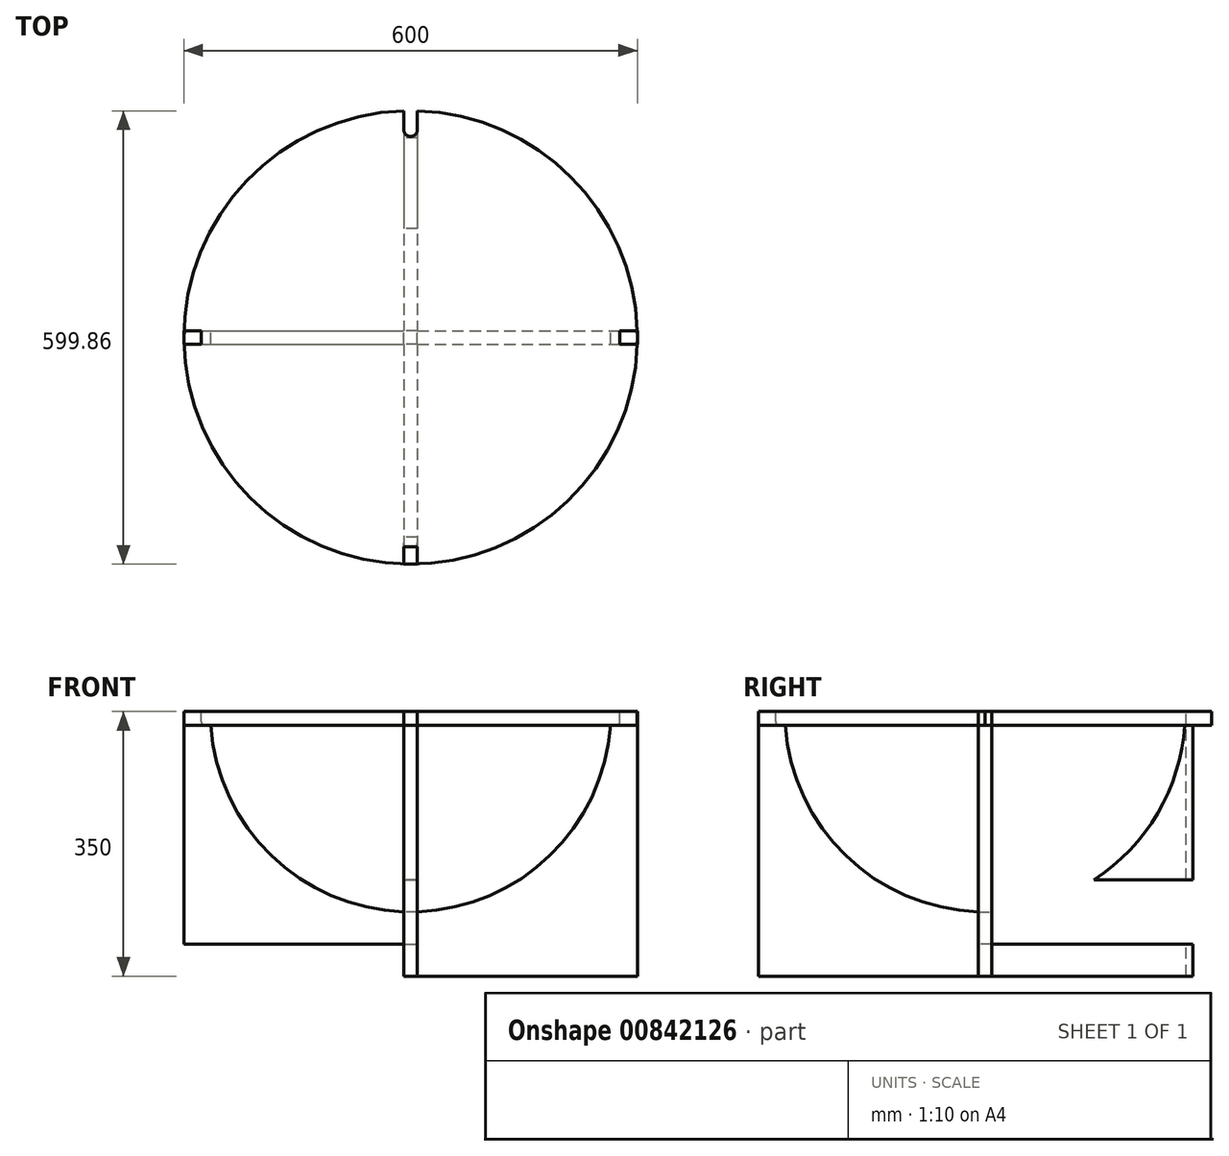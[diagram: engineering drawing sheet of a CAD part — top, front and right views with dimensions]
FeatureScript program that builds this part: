
annotation { "Feature Type Name" : "Feature", "Feature Type Description" : "" }
export const myFeature = defineFeature(function(context is Context, id is Id, definition is map)
    precondition{}
    {
        {
            var Q0;
            Q0=qCreatedBy(makeId("Front.planeOp"),FACE);
            var sketch = newSketch(context, id + "F0", { "sketchPlane" : qUnion([Q0])});
            skLineSegment(sketch, "E0.bottom", {"start": v(-300, -175) * mm, "end": v(140, -175) * mm});
            skLineSegment(sketch, "E0.top", {"start": v(-300, 175) * mm, "end": v(-277, 175) * mm});
            skLineSegment(sketch, "E0.left", {"start": v(-300, -175) * mm, "end": v(-300, 175) * mm});
            skLineSegment(sketch, "E0.right", {"start": v(300, -175) * mm, "end": v(300, 175) * mm});
            skPoint(sketch, "E0.middle", {"position": v(0, 0) * mm});
            skArc(sketch, "E1", {"start": v(-264.39, 157) * mm, "mid": v(0, -90) * mm, "end": v(264.39, 157) * mm});
            skLineSegment(sketch, "E2.trimOffspring", {"start": v(277, 175) * mm, "end": v(300, 175) * mm});
            skLineSegment(sketch, "E3.trimOffspring", {"start": v(140, -175) * mm, "end": v(300, -175) * mm});
            skLineSegment(sketch, "E4.bottom", {"start": v(-277, 157) * mm, "end": v(-264.39, 157) * mm});
            skLineSegment(sketch, "E4.left", {"start": v(-277, 157) * mm, "end": v(-277, 175) * mm});
            skLineSegment(sketch, "E4.right", {"start": v(277, 157) * mm, "end": v(277, 175) * mm});
            skPoint(sketch, "E5.orphan", {"position": v(-277, 193) * mm});
            skLineSegment(sketch, "E6.trimOffspring", {"start": v(264.39, 157) * mm, "end": v(277, 157) * mm});
            skPoint(sketch, "E7.orphan", {"position": v(277, 193) * mm});
            skSolve(sketch);
        }
        {
            var Q0;
            Q0=qSketchRegion(id+"F0",true);
            extrude(context, id + "F1", {"entities" : qUnion([Q0]), "depth" : 9 * mm, "offsetDistance" : 25 * mm, "hasSecondDirection" : true, "secondDirectionOppositeDirection" : true, "secondDirectionDepth" : 9 * mm});
        }
        {
            var Q0;
            Q0=qCreatedBy(makeId("Right.planeOp"),FACE);
            var Q1;
            Q1=qCreatedBy(makeId("Front.planeOp"),FACE);
            cPlane(context, id + "F2", {"entities" : qUnion([Q0, Q1]), "cplaneType" : CPlaneType.MID_PLANE, "offset" : 25 * mm, "width" : 150 * mm, "height" : 150 * mm});
        }
        {
            var Q0;
            Q0=makeQuery(id+"F1.opExtrude","SWEPT_BODY",BODY,{"disambiguationData":[OSD([sQuery(id+"F0.wireOp",EDGE,"E0.bottom"),sQuery(id+"F0.wireOp",EDGE,"E0.top"),sQuery(id+"F0.wireOp",EDGE,"E0.left"),sQuery(id+"F0.wireOp",EDGE,"E0.right"),sQuery(id+"F0.wireOp",EDGE,"E1"),sQuery(id+"F0.wireOp",EDGE,"EXiE6QKu-Vo7E-oY48-lKYo-ds7yFPW4EHc2"),sQuery(id+"F0.wireOp",EDGE,"E2.trimOffspring"),sQuery(id+"F0.wireOp",EDGE,"E3.trimOffspring")])]});
            var Q1;
            Q1=qCreatedBy(id+"F2.planeOp",FACE);
            mirror(context, id + "F3", {"entities" : qUnion([Q0]), "mirrorPlane" : qUnion([Q1])});
        }
        {
            var Q0;
            Q0=makeQuery(id+"F1.opExtrude","SWEPT_FACE",FACE,{"disambiguationData":[OSD([sQuery(id+"F0.wireOp",EDGE,"E2.trimOffspring")])]});
            var sketch = newSketch(context, id + "F4", { "sketchPlane" : qUnion([Q0])});
            skCircle(sketch, "E8", {"center": v(0, 0) * mm, "radius": 300 * mm});
            skSolve(sketch);
        }
        {
            var Q0;
            {var subQ1=sQuery(id+"F0.wireOp",EDGE,"E2.trimOffspring");var subQ6=makeQuery(id+"F1.opExtrude","SWEPT_EDGE",EDGE,{"disambiguationData":[OSD([sQuery(id+"F0.wireOp",EDGE,"E1"),subQ1])]});Q0=makeQuery(id+"F4.imprint","IMPRINT",FACE,{"disambiguationData":[TD([[makeQuery(id+"F4.imprint","IMPRINT",EDGE,{"derivedFrom":subQ6}),1.0]])]});}
            var Q1;
            {var subQ1=sQuery(id+"F0.wireOp",EDGE,"E2.trimOffspring");var subQ6=makeQuery(id+"F1.opExtrude","SWEPT_EDGE",EDGE,{"disambiguationData":[OSD([subQ1,sQuery(id+"F0.wireOp",EDGE,"E4.right")])]});Q1=makeQuery(id+"F4.imprint","IMPRINT",FACE,{"disambiguationData":[TD([[makeQuery(id+"F4.imprint","IMPRINT",EDGE,{"derivedFrom":subQ6}),1.0]])]});}
            extrude(context, id + "F5", {"entities" : qUnion([Q0, Q1]), "oppositeDirection" : true, "depth" : 18 * mm, "offsetDistance" : 25 * mm});
        }
        {
            var Q0;
            Q0=makeQuery(id+"F5.opExtrude","CAP_FACE",FACE,{"disambiguationData":[OSD([sQuery(id+"F0.wireOp",EDGE,"E1"),sQuery(id+"F0.wireOp",EDGE,"E2.trimOffspring"),sQuery(id+"F4.wireOp",EDGE,"E8")])],"isStart":true});
            var sketch = newSketch(context, id + "F6", { "sketchPlane" : qUnion([Q0])});
            skLineSegment(sketch, "E9.top", {"start": v(9, 325) * mm, "end": v(-9, 325) * mm});
            skLineSegment(sketch, "E9.left", {"start": v(9, 275) * mm, "end": v(9, 325) * mm});
            skLineSegment(sketch, "E9.right", {"start": v(-9, 275) * mm, "end": v(-9, 325) * mm});
            skPoint(sketch, "E9.middle", {"position": v(0, 300) * mm});
            skArc(sketch, "E10", {"start": v(-9, 275) * mm, "mid": v(0, 266) * mm, "end": v(9, 275) * mm});
            skSolve(sketch);
        }
        {
            var Q0;
            Q0=qSketchRegion(id+"F6",true);
            extrude(context, id + "F7", {"entities" : qUnion([Q0]), "operationType" : NewBodyOperationType.REMOVE, "endBound" : BoundingType.THROUGH_ALL, "oppositeDirection" : true, "depth" : 25 * mm, "offsetDistance" : 25 * mm});
        }
        {
            var Q0;
            Q0=makeQuery(id+"F1.opExtrude","SWEPT_EDGE",EDGE,{"disambiguationData":[OSD([sQuery(id+"F0.wireOp",EDGE,"E4.bottom"),sQuery(id+"F0.wireOp",EDGE,"E4.left")])]});
            var Q1;
            Q1=makeQuery(id+"F3.opPattern","COPY",EDGE,{"derivedFrom":makeQuery(id+"F1.opExtrude","SWEPT_EDGE",EDGE,{"disambiguationData":[OSD([sQuery(id+"F0.wireOp",EDGE,"E4.bottom"),sQuery(id+"F0.wireOp",EDGE,"E4.left")])]}),"instanceName":"1"});
            var Q2;
            Q2=makeQuery(id+"F1.opExtrude","SWEPT_EDGE",EDGE,{"disambiguationData":[OSD([sQuery(id+"F0.wireOp",EDGE,"E4.right"),sQuery(id+"F0.wireOp",EDGE,"E6.trimOffspring")])]});
            var Q3;
            Q3=makeQuery(id+"F3.opPattern","COPY",EDGE,{"derivedFrom":makeQuery(id+"F1.opExtrude","SWEPT_EDGE",EDGE,{"disambiguationData":[OSD([sQuery(id+"F0.wireOp",EDGE,"E4.right"),sQuery(id+"F0.wireOp",EDGE,"E6.trimOffspring")])]}),"instanceName":"1"});
            fillet(context, id + "F8", {"entities" : qUnion([Q0, Q1, Q2, Q3]), "radius" : 5 * mm, "tangentPropagation" : true, "allowEdgeOverflow" : false});
        }
        {
            var Q0;
            {var subQ0=sQuery(id+"F0.wireOp",EDGE,"E2.trimOffspring");var subQ1=sQuery(id+"F0.wireOp",EDGE,"EXiE6QKu-Vo7E-oY48-lKYo-ds7yFPW4EHc2");var subQ3=sQuery(id+"F0.wireOp",EDGE,"E1");var subQ5=sQuery(id+"F0.wireOp",EDGE,"E0.right");var subQ6=sQuery(id+"F0.wireOp",EDGE,"E3.trimOffspring");var subQ7=makeQuery(id+"F1.opExtrude","CAP_FACE",FACE,{"disambiguationData":[OSD([sQuery(id+"F0.wireOp",EDGE,"E0.bottom"),sQuery(id+"F0.wireOp",EDGE,"E0.top"),sQuery(id+"F0.wireOp",EDGE,"E0.left"),subQ5,subQ3,subQ1,subQ0,subQ6])],"isStart":false});Q0=makeQuery(id+"F3.boolean.opBoolean","SPLIT",FACE,{"disambiguationData":[TD([makeQuery(id+"F1.opExtrude","SWEPT_FACE",FACE,{"disambiguationData":[OSD([subQ5])]})])],"derivedFrom":subQ7});}
            var sketch = newSketch(context, id + "F9", { "sketchPlane" : qUnion([Q0])});
            skLineSegment(sketch, "E11.bottom", {"start": v(9, -132.5) * mm, "end": v(-9, -132.5) * mm});
            skLineSegment(sketch, "E11.top", {"start": v(9, -47.5) * mm, "end": v(-9, -47.5) * mm});
            skLineSegment(sketch, "E11.left", {"start": v(9, -132.5) * mm, "end": v(9, -47.5) * mm});
            skLineSegment(sketch, "E11.right", {"start": v(-9, -132.5) * mm, "end": v(-9, -47.5) * mm});
            skPoint(sketch, "E11.middle", {"position": v(0, -90) * mm});
            skSolve(sketch);
        }
        {
            var Q0;
            Q0=qSketchRegion(id+"F9",true);
            extrude(context, id + "F10", {"entities" : qUnion([Q0]), "operationType" : NewBodyOperationType.REMOVE, "endBound" : BoundingType.THROUGH_ALL, "oppositeDirection" : true, "depth" : 25 * mm, "offsetDistance" : 25 * mm});
        }
        {
            var Q0;
            Q0=makeQuery(id+"F3.opPattern","COPY",FACE,{"derivedFrom":makeQuery(id+"F1.opExtrude","CAP_FACE",FACE,{"disambiguationData":[OSD([sQuery(id+"F0.wireOp",EDGE,"E0.bottom"),sQuery(id+"F0.wireOp",EDGE,"E0.top"),sQuery(id+"F0.wireOp",EDGE,"E0.left"),sQuery(id+"F0.wireOp",EDGE,"E0.right"),sQuery(id+"F0.wireOp",EDGE,"E1"),sQuery(id+"F0.wireOp",EDGE,"EXiE6QKu-Vo7E-oY48-lKYo-ds7yFPW4EHc2"),sQuery(id+"F0.wireOp",EDGE,"E2.trimOffspring"),sQuery(id+"F0.wireOp",EDGE,"E3.trimOffspring")])],"isStart":false}),"instanceName":"1"});
            var sketch = newSketch(context, id + "F11", { "sketchPlane" : qUnion([Q0])});
            skLineSegment(sketch, "E12.bottom", {"start": v(9, -217.5) * mm, "end": v(-9, -217.5) * mm});
            skLineSegment(sketch, "E12.top", {"start": v(9, -132.5) * mm, "end": v(-9, -132.5) * mm});
            skLineSegment(sketch, "E12.left", {"start": v(9, -217.5) * mm, "end": v(9, -132.5) * mm});
            skLineSegment(sketch, "E12.right", {"start": v(-9, -217.5) * mm, "end": v(-9, -132.5) * mm});
            skPoint(sketch, "E12.middle", {"position": v(0, -175) * mm});
            skSolve(sketch);
        }
        {
            var Q0;
            Q0=qSketchRegion(id+"F11",true);
            extrude(context, id + "F12", {"entities" : qUnion([Q0]), "operationType" : NewBodyOperationType.REMOVE, "endBound" : BoundingType.THROUGH_ALL, "oppositeDirection" : true, "depth" : 25 * mm, "offsetDistance" : 25 * mm});
        }
    });
